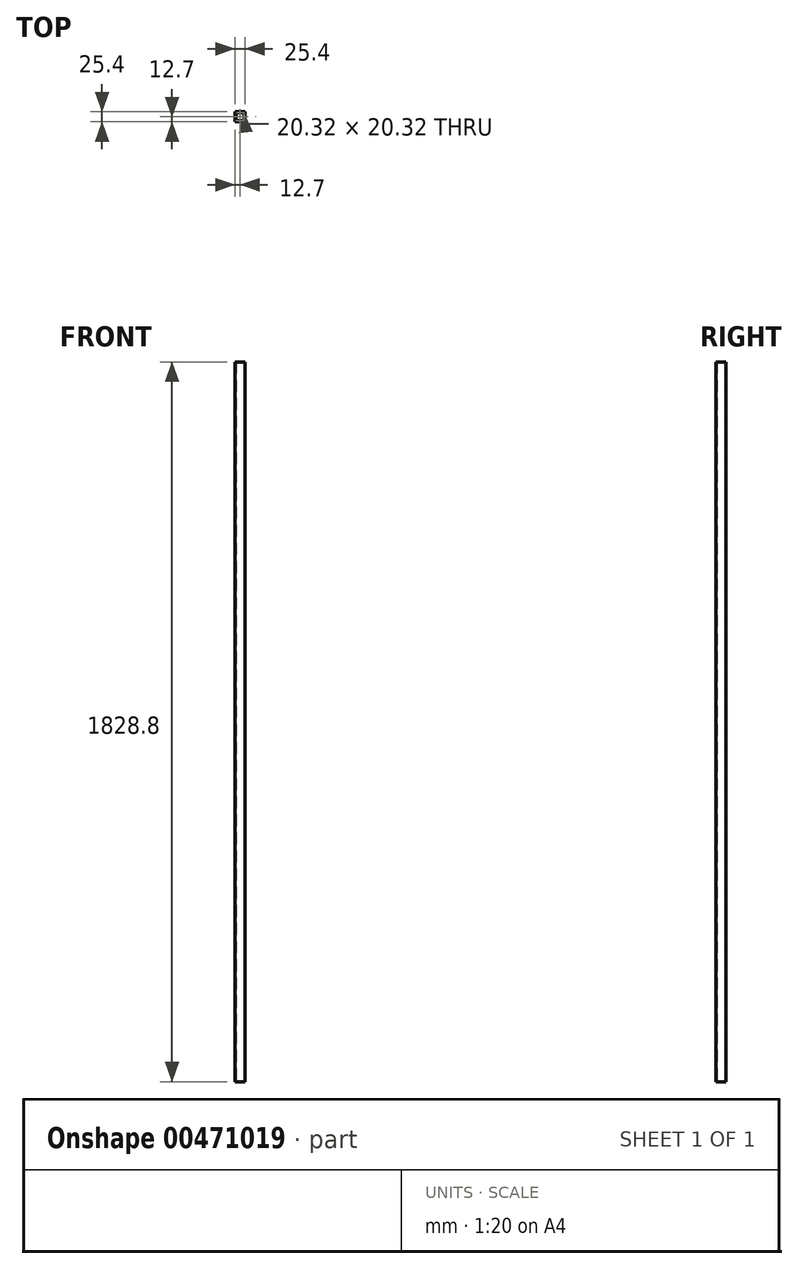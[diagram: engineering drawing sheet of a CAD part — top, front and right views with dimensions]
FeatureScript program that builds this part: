
annotation { "Feature Type Name" : "Feature", "Feature Type Description" : "" }
export const myFeature = defineFeature(function(context is Context, id is Id, definition is map)
    precondition{}
    {
        {
            var Q0;
            Q0=qCreatedBy(makeId("Top.planeOp"),FACE);
            var sketch = newSketch(context, id + "F0", { "sketchPlane" : qUnion([Q0])});
            skLineSegment(sketch, "E0.bottom", {"start": v(-12.7, -12.7) * mm, "end": v(12.7, -12.7) * mm});
            skLineSegment(sketch, "E0.top", {"start": v(-12.7, 12.7) * mm, "end": v(12.7, 12.7) * mm});
            skLineSegment(sketch, "E0.left", {"start": v(-12.7, -12.7) * mm, "end": v(-12.7, 12.7) * mm});
            skLineSegment(sketch, "E0.right", {"start": v(12.7, -12.7) * mm, "end": v(12.7, 12.7) * mm});
            skPoint(sketch, "E0.middle", {"position": v(0, 0) * mm});
            skLineSegment(sketch, "E1.bottom", {"start": v(-10.16, -10.16) * mm, "end": v(10.16, -10.16) * mm});
            skLineSegment(sketch, "E1.top", {"start": v(-10.16, 10.16) * mm, "end": v(10.16, 10.16) * mm});
            skLineSegment(sketch, "E1.left", {"start": v(-10.16, -10.16) * mm, "end": v(-10.16, 10.16) * mm});
            skLineSegment(sketch, "E1.right", {"start": v(10.16, -10.16) * mm, "end": v(10.16, 10.16) * mm});
            skSolve(sketch);
        }
        {
            var Q0;
            Q0=makeQuery(id+"F0.imprint","IMPRINT",FACE,{"disambiguationData":[TD([[makeQuery(id+"F0.imprint","IMPRINT",EDGE,{"derivedFrom":sQuery(id+"F0.wireOp",EDGE,"E0.bottom")}),1.0]])]});
            extrude(context, id + "F1", {"entities" : qUnion([Q0]), "endBound" : BoundingType.SYMMETRIC, "depth" : 1828.8 * mm});
        }
    });
